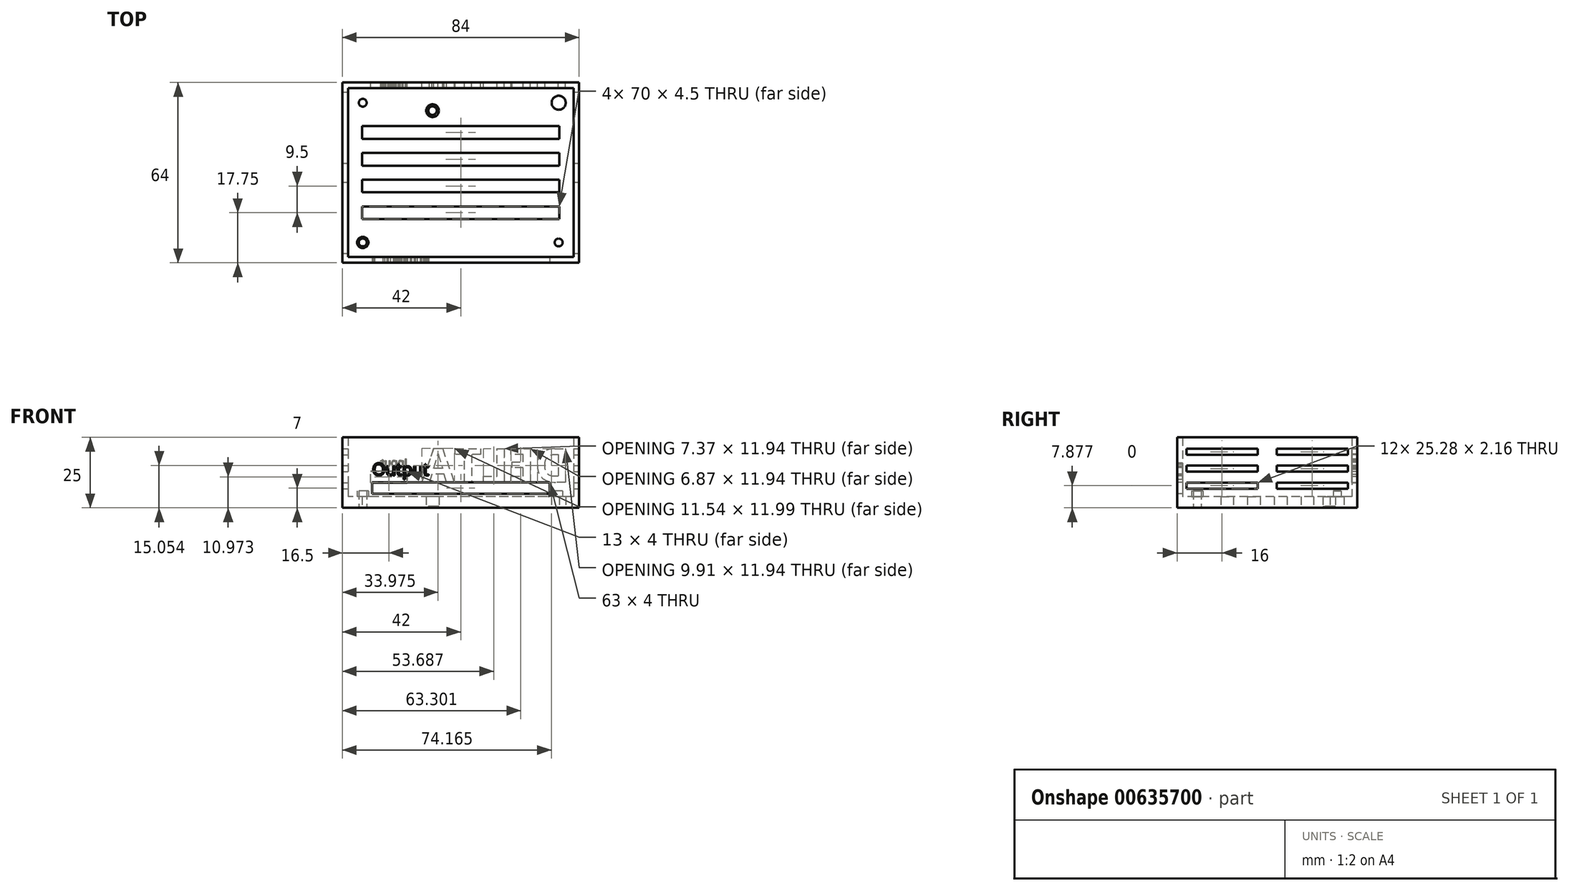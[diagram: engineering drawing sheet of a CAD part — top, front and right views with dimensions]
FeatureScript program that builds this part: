
annotation { "Feature Type Name" : "Feature", "Feature Type Description" : "" }
export const myFeature = defineFeature(function(context is Context, id is Id, definition is map)
    precondition{}
    {
        {
            var Q0;
            Q0=qCreatedBy(makeId("Top.planeOp"),FACE);
            var sketch = newSketch(context, id + "F0", { "sketchPlane" : qUnion([Q0])});
            skLineSegment(sketch, "E0.bottom", {"start": v(40, 30) * mm, "end": v(-40, 30) * mm});
            skLineSegment(sketch, "E0.top", {"start": v(40, -30) * mm, "end": v(-40, -30) * mm});
            skLineSegment(sketch, "E0.left", {"start": v(40, 30) * mm, "end": v(40, -30) * mm});
            skLineSegment(sketch, "E0.right", {"start": v(-40, 30) * mm, "end": v(-40, -30) * mm});
            skPoint(sketch, "E0.middle", {"position": v(0, 0) * mm});
            skCircle(sketch, "E1", {"center": v(-34.75, 24.8) * mm, "radius": 2 * mm});
            skCircle(sketch, "E2.MirrorC", {"center": v(34.75, 24.8) * mm, "radius": 2.5 * mm});
            skCircle(sketch, "E3.MirrorC", {"center": v(-34.75, -24.8) * mm, "radius": 2 * mm});
            skCircle(sketch, "E4.MirrorC", {"center": v(34.75, -24.8) * mm, "radius": 2.5 * mm});
            skCircle(sketch, "E5", {"center": v(-34.75, 24.8) * mm, "radius": 1.4 * mm});
            skCircle(sketch, "E6.MirrorC", {"center": v(-34.75, -24.8) * mm, "radius": 1.4 * mm});
            skCircle(sketch, "E7.MirrorC", {"center": v(34.75, 24.8) * mm, "radius": 1.4 * mm});
            skCircle(sketch, "E8.MirrorC", {"center": v(34.75, -24.8) * mm, "radius": 1.4 * mm});
            skLineSegment(sketch, "E9.bottom", {"start": v(42, 32) * mm, "end": v(-42, 32) * mm});
            skLineSegment(sketch, "E9.top", {"start": v(42, -32) * mm, "end": v(-42, -32) * mm});
            skLineSegment(sketch, "E9.left", {"start": v(42, 32) * mm, "end": v(42, -32) * mm});
            skLineSegment(sketch, "E9.right", {"start": v(-42, 32) * mm, "end": v(-42, -32) * mm});
            skCircle(sketch, "E10", {"center": v(-10, 22) * mm, "radius": 1.5 * mm});
            skCircle(sketch, "E11", {"center": v(-10, 22) * mm, "radius": 2.25 * mm});
            skLineSegment(sketch, "E12.bottom", {"start": v(35, 16.5) * mm, "end": v(-35, 16.5) * mm});
            skLineSegment(sketch, "E12.top", {"start": v(35, 12) * mm, "end": v(-35, 12) * mm});
            skLineSegment(sketch, "E12.left", {"start": v(35, 16.5) * mm, "end": v(35, 12) * mm});
            skLineSegment(sketch, "E12.right", {"start": v(-35, 16.5) * mm, "end": v(-35, 12) * mm});
            skPoint(sketch, "E12.middle", {"position": v(0, 14.25) * mm});
            skLineSegment(sketch, "E13.bottom", {"start": v(35, 7) * mm, "end": v(-35, 7) * mm});
            skLineSegment(sketch, "E13.top", {"start": v(35, 2.5) * mm, "end": v(-35, 2.5) * mm});
            skLineSegment(sketch, "E13.left", {"start": v(35, 7) * mm, "end": v(35, 2.5) * mm});
            skLineSegment(sketch, "E13.right", {"start": v(-35, 7) * mm, "end": v(-35, 2.5) * mm});
            skPoint(sketch, "E13.middle", {"position": v(0, 4.75) * mm});
            skLineSegment(sketch, "E14.MirrorCS", {"start": v(-35, -7) * mm, "end": v(-35, -2.5) * mm});
            skLineSegment(sketch, "E15.MirrorCS", {"start": v(35, -12) * mm, "end": v(-35, -12) * mm});
            skPoint(sketch, "E16.MirrorP", {"position": v(0, -4.75) * mm});
            skLineSegment(sketch, "E17.MirrorCS", {"start": v(35, -7) * mm, "end": v(-35, -7) * mm});
            skLineSegment(sketch, "E18.MirrorCS", {"start": v(35, -2.5) * mm, "end": v(-35, -2.5) * mm});
            skLineSegment(sketch, "E19.MirrorCS", {"start": v(35, -16.5) * mm, "end": v(35, -12) * mm});
            skLineSegment(sketch, "E20.MirrorCS", {"start": v(35, -16.5) * mm, "end": v(-35, -16.5) * mm});
            skLineSegment(sketch, "E21.MirrorCS", {"start": v(-35, -16.5) * mm, "end": v(-35, -12) * mm});
            skLineSegment(sketch, "E22.MirrorCS", {"start": v(35, -7) * mm, "end": v(35, -2.5) * mm});
            skPoint(sketch, "E23.MirrorP", {"position": v(0, -14.25) * mm});
            skSolve(sketch);
        }
        {
            var Q0;
            Q0=makeQuery(id+"F0.imprint","IMPRINT",FACE,{"disambiguationData":[TD([[makeQuery(id+"F0.imprint","IMPRINT",EDGE,{"derivedFrom":sQuery(id+"F0.wireOp",EDGE,"E0.bottom")}),1.0]])]});
            extrude(context, id + "F1", {"entities" : qUnion([Q0]), "depth" : 1 * mm, "offsetDistance" : 25 * mm});
        }
        {
            var Q0;
            Q0=makeQuery(id+"F0.imprint","IMPRINT",FACE,{"disambiguationData":[TD([[makeQuery(id+"F0.imprint","IMPRINT",EDGE,{"derivedFrom":sQuery(id+"F0.wireOp",EDGE,"E3.MirrorC")}),-1.0]])]});
            var Q1;
            Q1=makeQuery(id+"F0.imprint","IMPRINT",FACE,{"disambiguationData":[TD([[makeQuery(id+"F0.imprint","IMPRINT",EDGE,{"derivedFrom":sQuery(id+"F0.wireOp",EDGE,"E1")}),1.0]])]});
            var Q2;
            Q2=makeQuery(id+"F0.imprint","IMPRINT",FACE,{"disambiguationData":[TD([[makeQuery(id+"F0.imprint","IMPRINT",EDGE,{"derivedFrom":sQuery(id+"F0.wireOp",EDGE,"E2.MirrorC")}),-1.0]])]});
            var Q3;
            Q3=makeQuery(id+"F0.imprint","IMPRINT",FACE,{"disambiguationData":[TD([[makeQuery(id+"F0.imprint","IMPRINT",EDGE,{"derivedFrom":sQuery(id+"F0.wireOp",EDGE,"E4.MirrorC")}),1.0]])]});
            extrude(context, id + "F2", {"entities" : qUnion([Q0, Q1, Q2, Q3]), "operationType" : NewBodyOperationType.ADD, "depth" : 4 * mm, "offsetDistance" : 25 * mm});
        }
        {
            var Q0;
            Q0=makeQuery(id+"F0.imprint","IMPRINT",FACE,{"disambiguationData":[TD([[makeQuery(id+"F0.imprint","IMPRINT",EDGE,{"derivedFrom":sQuery(id+"F0.wireOp",EDGE,"E5")}),1.0]])]});
            var Q1;
            Q1=makeQuery(id+"F0.imprint","IMPRINT",FACE,{"disambiguationData":[TD([[makeQuery(id+"F0.imprint","IMPRINT",EDGE,{"derivedFrom":sQuery(id+"F0.wireOp",EDGE,"E6.MirrorC")}),-1.0]])]});
            var Q2;
            Q2=makeQuery(id+"F0.imprint","IMPRINT",FACE,{"disambiguationData":[TD([[makeQuery(id+"F0.imprint","IMPRINT",EDGE,{"derivedFrom":sQuery(id+"F0.wireOp",EDGE,"E8.MirrorC")}),1.0]])]});
            extrude(context, id + "F3", {"entities" : qUnion([Q0, Q1, Q2]), "operationType" : NewBodyOperationType.ADD, "depth" : 6 * mm, "offsetDistance" : 25 * mm});
        }
        {
            var Q0;
            Q0=makeQuery(id+"F0.imprint","IMPRINT",FACE,{"disambiguationData":[TD([[makeQuery(id+"F0.imprint","IMPRINT",EDGE,{"derivedFrom":sQuery(id+"F0.wireOp",EDGE,"E0.bottom")}),-1.0]])]});
            extrude(context, id + "F4", {"entities" : qUnion([Q0]), "operationType" : NewBodyOperationType.ADD, "depth" : 25 * mm, "offsetDistance" : 25 * mm});
        }
        {
            var Q0;
            Q0=makeQuery(id+"F4.opExtrude","SWEPT_FACE",FACE,{"disambiguationData":[OSD([sQuery(id+"F0.wireOp",EDGE,"E9.top")])]});
            var sketch = newSketch(context, id + "F5", { "sketchPlane" : qUnion([Q0])});
            skLineSegment(sketch, "E24.bottom", {"start": v(31.5, 9) * mm, "end": v(-31.5, 9) * mm});
            skLineSegment(sketch, "E24.top", {"start": v(31.5, 5) * mm, "end": v(-31.5, 5) * mm});
            skLineSegment(sketch, "E24.left", {"start": v(31.5, 9) * mm, "end": v(31.5, 5) * mm});
            skLineSegment(sketch, "E24.right", {"start": v(-31.5, 9) * mm, "end": v(-31.5, 5) * mm});
            skPoint(sketch, "E24.middle", {"position": v(0, 7) * mm});
            skText(sketch, "E25", { "text": "Output\n", "fontName": "OpenSans-Regular.ttf"});
            const initialGuessF5  = {"E25": [-0.0314, 0.0115, 1, 0, 0.00436]};
            skSetInitialGuess(sketch, initialGuessF5);
            skSolve(sketch);
        }
        {
            var Q0;
            Q0 = qSketchRegion(id + "F5", true);
            extrude(context, id + "F6", {"entities" : qUnion([Q0]), "operationType" : NewBodyOperationType.REMOVE, "oppositeDirection" : true, "depth" : 25 * mm, "offsetDistance" : 25 * mm});
        }
        {
            var Q0;
            Q0=makeQuery(id+"F4.opExtrude","SWEPT_FACE",FACE,{"disambiguationData":[OSD([sQuery(id+"F0.wireOp",EDGE,"E9.bottom")])]});
            var sketch = newSketch(context, id + "F7", { "sketchPlane" : qUnion([Q0])});
            skLineSegment(sketch, "E26.bottom", {"start": v(32, 12.97) * mm, "end": v(19, 12.97) * mm});
            skLineSegment(sketch, "E26.top", {"start": v(32, 8.97) * mm, "end": v(19, 8.97) * mm});
            skLineSegment(sketch, "E26.left", {"start": v(32, 12.97) * mm, "end": v(32, 8.97) * mm});
            skLineSegment(sketch, "E26.right", {"start": v(19, 12.97) * mm, "end": v(19, 8.97) * mm});
            skPoint(sketch, "E26.middle", {"position": v(25.5, 10.97) * mm});
            skText(sketch, "E27", { "text": "DELTA", "fontName": "OpenSans-Bold.ttf"});
            skText(sketch, "E28", { "text": "Input\n", "fontName": "OpenSans-Regular.ttf"});
            const initialGuessF7  = {"E27": [-0.03862, 0.00906, 1, 0, 0.01204], "E28": [0.019, 0.0147, 1, 0, 0.00276]};
            skSetInitialGuess(sketch, initialGuessF7);
            skSolve(sketch);
        }
        {
            var Q0;
            Q0 = qSketchRegion(id + "F7", true);
            extrude(context, id + "F8", {"entities" : qUnion([Q0]), "operationType" : NewBodyOperationType.REMOVE, "oppositeDirection" : true, "depth" : 25 * mm, "offsetDistance" : 25 * mm});
        }
        {
            var Q0;
            Q0=makeQuery(id+"F4.opExtrude","SWEPT_FACE",FACE,{"disambiguationData":[OSD([sQuery(id+"F0.wireOp",EDGE,"E9.left")])]});
            var sketch = newSketch(context, id + "F9", { "sketchPlane" : qUnion([Q0])});
            skLineSegment(sketch, "E29.bottom", {"start": v(-3.36, 20.96) * mm, "end": v(-28.64, 20.96) * mm});
            skLineSegment(sketch, "E29.top", {"start": v(-3.36, 18.8) * mm, "end": v(-28.64, 18.8) * mm});
            skLineSegment(sketch, "E29.left", {"start": v(-3.36, 20.96) * mm, "end": v(-3.36, 18.8) * mm});
            skLineSegment(sketch, "E29.right", {"start": v(-28.64, 20.96) * mm, "end": v(-28.64, 18.8) * mm});
            skPoint(sketch, "E29.middle", {"position": v(-16, 19.88) * mm});
            skLineSegment(sketch, "E30.bottom", {"start": v(-3.36, 14.96) * mm, "end": v(-28.64, 14.96) * mm});
            skLineSegment(sketch, "E30.top", {"start": v(-3.36, 12.8) * mm, "end": v(-28.64, 12.8) * mm});
            skLineSegment(sketch, "E30.left", {"start": v(-3.36, 14.96) * mm, "end": v(-3.36, 12.8) * mm});
            skLineSegment(sketch, "E30.right", {"start": v(-28.64, 14.96) * mm, "end": v(-28.64, 12.8) * mm});
            skPoint(sketch, "E30.middle", {"position": v(-16, 13.88) * mm});
            skLineSegment(sketch, "E31.bottom", {"start": v(-3.36, 8.96) * mm, "end": v(-28.64, 8.96) * mm});
            skLineSegment(sketch, "E31.top", {"start": v(-3.36, 6.8) * mm, "end": v(-28.64, 6.8) * mm});
            skLineSegment(sketch, "E31.left", {"start": v(-3.36, 8.96) * mm, "end": v(-3.36, 6.8) * mm});
            skLineSegment(sketch, "E31.right", {"start": v(-28.64, 8.96) * mm, "end": v(-28.64, 6.8) * mm});
            skPoint(sketch, "E31.middle", {"position": v(-16, 7.88) * mm});
            skLineSegment(sketch, "E32.MirrorCS", {"start": v(3.36, 8.96) * mm, "end": v(3.36, 6.8) * mm});
            skLineSegment(sketch, "E33.MirrorCS", {"start": v(3.36, 20.96) * mm, "end": v(3.36, 18.8) * mm});
            skPoint(sketch, "E34.MirrorP", {"position": v(16, 19.88) * mm});
            skPoint(sketch, "E35.MirrorP", {"position": v(16, 13.88) * mm});
            skLineSegment(sketch, "E36.MirrorCS", {"start": v(28.64, 8.96) * mm, "end": v(28.64, 6.8) * mm});
            skPoint(sketch, "E37.MirrorP", {"position": v(16, 7.88) * mm});
            skLineSegment(sketch, "E38.MirrorCS", {"start": v(3.36, 8.96) * mm, "end": v(28.64, 8.96) * mm});
            skLineSegment(sketch, "E39.MirrorCS", {"start": v(28.64, 14.96) * mm, "end": v(28.64, 12.8) * mm});
            skLineSegment(sketch, "E40.MirrorCS", {"start": v(3.36, 14.96) * mm, "end": v(3.36, 12.8) * mm});
            skLineSegment(sketch, "E41.MirrorCS", {"start": v(3.36, 12.8) * mm, "end": v(28.64, 12.8) * mm});
            skLineSegment(sketch, "E42.MirrorCS", {"start": v(3.36, 18.8) * mm, "end": v(28.64, 18.8) * mm});
            skLineSegment(sketch, "E43.MirrorCS", {"start": v(28.64, 20.96) * mm, "end": v(28.64, 18.8) * mm});
            skLineSegment(sketch, "E44.MirrorCS", {"start": v(3.36, 14.96) * mm, "end": v(28.64, 14.96) * mm});
            skLineSegment(sketch, "E45.MirrorCS", {"start": v(3.36, 6.8) * mm, "end": v(28.64, 6.8) * mm});
            skLineSegment(sketch, "E46.MirrorCS", {"start": v(3.36, 20.96) * mm, "end": v(28.64, 20.96) * mm});
            skSolve(sketch);
        }
        {
            var Q0;
            Q0 = qSketchRegion(id + "F9", true);
            extrude(context, id + "F10", {"entities" : qUnion([Q0]), "operationType" : NewBodyOperationType.REMOVE, "oppositeDirection" : true, "depth" : 89.4 * mm, "offsetDistance" : 25 * mm});
        }
        {
            var Q0;
            Q0=makeQuery(id+"F0.imprint","IMPRINT",FACE,{"disambiguationData":[TD([[makeQuery(id+"F0.imprint","IMPRINT",EDGE,{"derivedFrom":sQuery(id+"F0.wireOp",EDGE,"E10")}),-1.0]])]});
            extrude(context, id + "F11", {"entities" : qUnion([Q0]), "operationType" : NewBodyOperationType.ADD, "depth" : .5 * mm, "offsetDistance" : 25 * mm});
        }
    });
